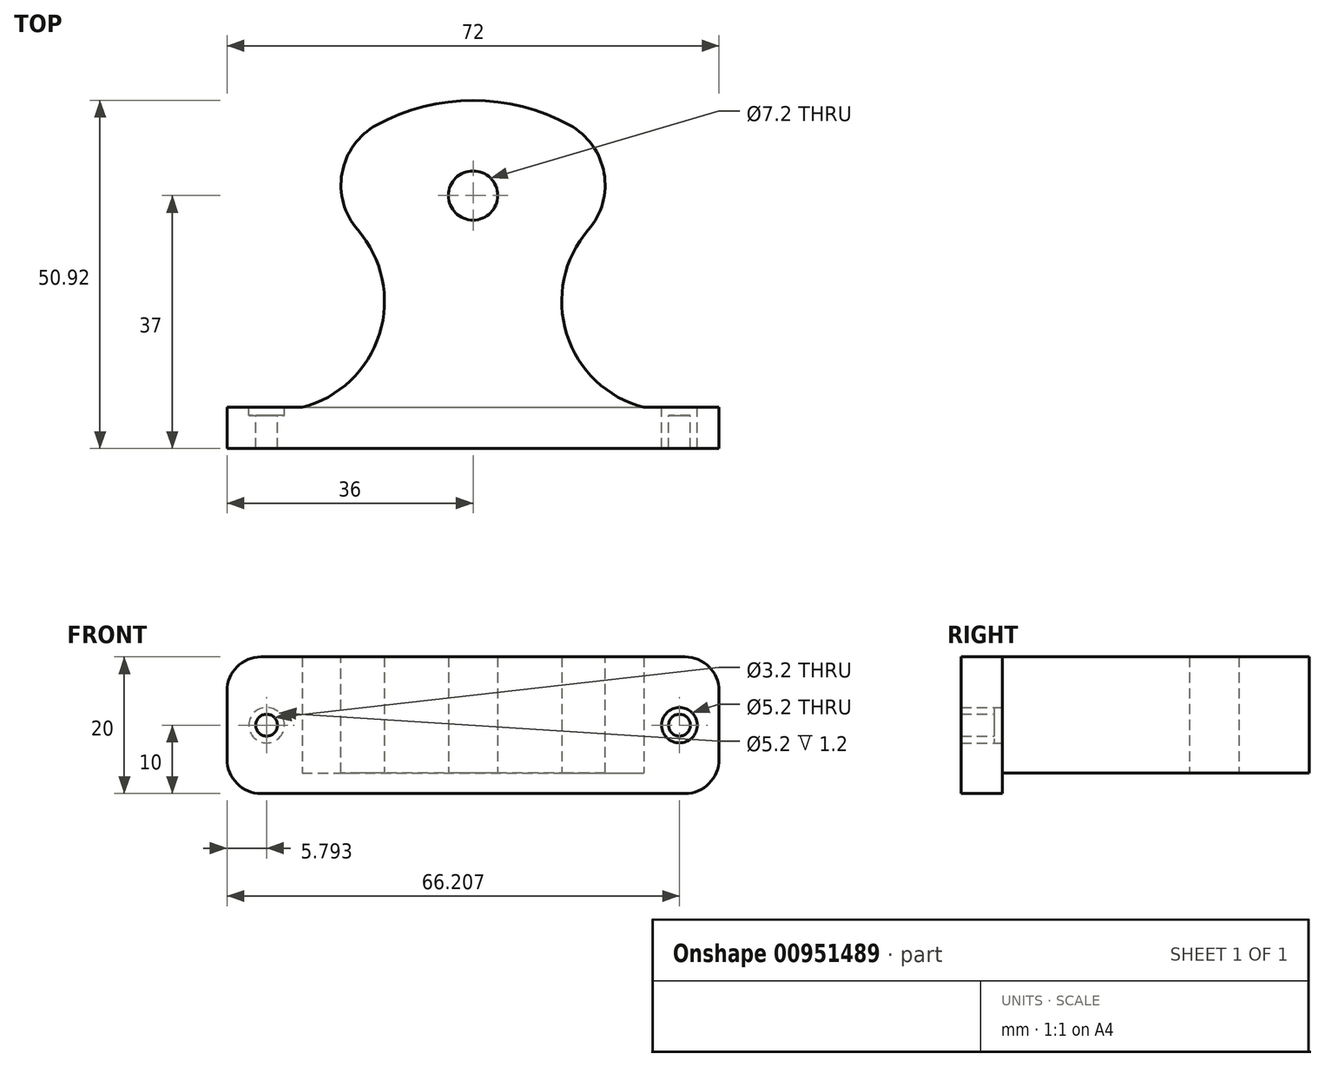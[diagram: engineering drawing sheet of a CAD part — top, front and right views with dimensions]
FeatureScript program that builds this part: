
annotation { "Feature Type Name" : "Feature", "Feature Type Description" : "" }
export const myFeature = defineFeature(function(context is Context, id is Id, definition is map)
    precondition{}
    {
        {
            var Q0;
            Q0=qCreatedBy(makeId("Top.planeOp"),FACE);
            var sketch = newSketch(context, id + "F0", { "sketchPlane" : qUnion([Q0])});
            skLineSegment(sketch, "E0.bottom", {"start": v(-25, 15.5) * mm, "end": v(25, 15.5) * mm});
            skLineSegment(sketch, "E0.top", {"start": v(-25, -15.5) * mm, "end": v(25, -15.5) * mm});
            skLineSegment(sketch, "E0.left", {"start": v(-25, 15.5) * mm, "end": v(-25, -15.5) * mm});
            skLineSegment(sketch, "E0.right", {"start": v(25, 15.5) * mm, "end": v(25, -15.5) * mm});
            skPoint(sketch, "E0.middle", {"position": v(0, 0) * mm});
            skCircle(sketch, "E1", {"center": v(0, 0) * mm, "radius": 29.42 * mm});
            skPoint(sketch, "E2", {"position": v(0, 15.5) * mm});
            skCircle(sketch, "E3", {"center": v(0, 15.5) * mm, "radius": 2.5 * mm});
            skLineSegment(sketch, "E4.bottom", {"start": v(-36, -15.5) * mm, "end": v(36, -15.5) * mm});
            skLineSegment(sketch, "E4.top", {"start": v(-36, -21.5) * mm, "end": v(36, -21.5) * mm});
            skLineSegment(sketch, "E4.left", {"start": v(-36, -15.5) * mm, "end": v(-36, -21.5) * mm});
            skLineSegment(sketch, "E4.right", {"start": v(36, -15.5) * mm, "end": v(36, -21.5) * mm});
            skPoint(sketch, "E4.middle", {"position": v(0, -18.5) * mm});
            skArc(sketch, "E5", {"start": v(-25, -15.5) * mm, "mid": v(-12.97, 0) * mm, "end": v(-25, 15.5) * mm});
            skArc(sketch, "E6.MirrorCS", {"start": v(25, -15.5) * mm, "mid": v(12.97, 0) * mm, "end": v(25, 15.5) * mm});
            skCircle(sketch, "E7", {"center": v(0, 15.5) * mm, "radius": 3.6 * mm});
            skSolve(sketch);
        }
        {
            var Q0;
            Q0=makeQuery(id+"F0.imprint","IMPRINT",FACE,{"disambiguationData":[TD([[makeQuery(id+"F0.imprint","IMPRINT",EDGE,{"derivedFrom":sQuery(id+"F0.wireOp",EDGE,"E0.top")}),1.0]])]});
            var Q1;
            {var subQ0=sQuery(id+"F0.wireOp",EDGE,"E7");var subQ1=sQuery(id+"F0.wireOp",EDGE,"E0.bottom");var subQ2=makeQuery(id+"F0.imprint","INTERSECT",VERTEX,{"disambiguationData":[OD(0.0)],"derivedFrom":[subQ1,subQ0]});Q1=makeQuery(id+"F0.imprint","IMPRINT",FACE,{"disambiguationData":[TD([[makeQuery(id+"F0.imprint","IMPRINT",EDGE,{"disambiguationData":[TD([[subQ2,1.0]])],"derivedFrom":subQ1}),1.0]])]});}
            var Q2;
            {var subQ5=sQuery(id+"F0.wireOp",EDGE,"E4.left");Q2=makeQuery(id+"F0.imprint","IMPRINT",FACE,{"disambiguationData":[TD([[makeQuery(id+"F0.imprint","IMPRINT",EDGE,{"derivedFrom":subQ5}),1.0]])]});}
            var Q3;
            {var subQ0=sQuery(id+"F0.wireOp",EDGE,"E0.top");Q3=makeQuery(id+"F0.imprint","IMPRINT",FACE,{"disambiguationData":[TD([[makeQuery(id+"F0.imprint","IMPRINT",EDGE,{"derivedFrom":subQ0}),-1.0]])]});}
            var Q4;
            {var subQ5=sQuery(id+"F0.wireOp",EDGE,"E4.right");Q4=makeQuery(id+"F0.imprint","IMPRINT",FACE,{"disambiguationData":[TD([[makeQuery(id+"F0.imprint","IMPRINT",EDGE,{"derivedFrom":subQ5}),-1.0]])]});}
            var Q5;
            Q5=makeQuery(id+"F0.imprint","IMPRINT",FACE,{"disambiguationData":[TD([[makeQuery(id+"F0.imprint","IMPRINT",EDGE,{"derivedFrom":sQuery(id+"F0.wireOp",EDGE,"E0.top")}),1.0]])]});
            var Q6;
            {var subQ0=sQuery(id+"F0.wireOp",EDGE,"E7");var subQ1=sQuery(id+"F0.wireOp",EDGE,"E0.bottom");var subQ2=makeQuery(id+"F0.imprint","INTERSECT",VERTEX,{"disambiguationData":[OD(0.0)],"derivedFrom":[subQ1,subQ0]});Q6=makeQuery(id+"F0.imprint","IMPRINT",FACE,{"disambiguationData":[TD([[makeQuery(id+"F0.imprint","IMPRINT",EDGE,{"disambiguationData":[TD([[subQ2,-1.0]])],"derivedFrom":subQ0}),-1.0]])]});}
            var Q7;
            {var subQ0=sQuery(id+"F0.wireOp",EDGE,"E7");var subQ1=sQuery(id+"F0.wireOp",EDGE,"E0.bottom");var subQ2=makeQuery(id+"F0.imprint","INTERSECT",VERTEX,{"disambiguationData":[OD(0.0)],"derivedFrom":[subQ1,subQ0]});Q7=makeQuery(id+"F0.imprint","IMPRINT",FACE,{"disambiguationData":[TD([[makeQuery(id+"F0.imprint","IMPRINT",EDGE,{"disambiguationData":[TD([[subQ2,1.0]])],"derivedFrom":subQ1}),-1.0]])]});}
            extrude(context, id + "F1", {"entities" : qUnion([Q0, Q1, Q2, Q3, Q4, Q5, Q6, Q7]), "depth" : 20 * mm, "offsetDistance" : 25 * mm});
        }
        {
            var Q0;
            Q0=makeQuery(id+"F1.opExtrude","SWEPT_EDGE",EDGE,{"disambiguationData":[OSD([sQuery(id+"F0.wireOp",EDGE,"E0.bottom"),sQuery(id+"F0.wireOp",EDGE,"E0.right"),sQuery(id+"F0.wireOp",EDGE,"E1"),sQuery(id+"F0.wireOp",EDGE,"E6.MirrorCS")])]});
            var Q1;
            Q1=makeQuery(id+"F1.opExtrude","SWEPT_EDGE",EDGE,{"disambiguationData":[OSD([sQuery(id+"F0.wireOp",EDGE,"E0.bottom"),sQuery(id+"F0.wireOp",EDGE,"E0.left"),sQuery(id+"F0.wireOp",EDGE,"E1"),sQuery(id+"F0.wireOp",EDGE,"E5")])]});
            fillet(context, id + "F2", {"entities" : qUnion([Q0, Q1]), "radius" : 10 * mm, "tangentPropagation" : true, "allowEdgeOverflow" : false});
        }
        {
            var Q0;
            {var subQ0=sQuery(id+"F0.wireOp",EDGE,"E4.bottom");Q0=makeQuery(id+"F1.opExtrude","SWEPT_FACE",FACE,{"disambiguationData":[OSD([subQ0]),TDD([makeQuery(id+"F0.imprint","IMPRINT",EDGE,{"disambiguationData":[TD([[makeQuery(id+"F0.imprint","INTERSECT",VERTEX,{"derivedFrom":[subQ0,sQuery(id+"F0.wireOp",EDGE,"E4.left")]}),-1.0]])],"derivedFrom":subQ0})])]});}
            var sketch = newSketch(context, id + "F3", { "sketchPlane" : qUnion([Q0])});
            skCircle(sketch, "E8", {"center": v(30.2, 10) * mm, "radius": 1.6 * mm});
            skPoint(sketch, "E8.centerSnap0", {"position": v(25, 10) * mm});
            skCircle(sketch, "E9.MirrorC", {"center": v(-30.2, 10) * mm, "radius": 1.6 * mm});
            skCircle(sketch, "E10", {"center": v(-30.2, 10) * mm, "radius": 2.6 * mm});
            skCircle(sketch, "E11.MirrorC", {"center": v(30.2, 10) * mm, "radius": 2.6 * mm});
            skSolve(sketch);
        }
        {
            var Q0;
            Q0=makeQuery(id+"F3.imprint","IMPRINT",FACE,{"disambiguationData":[TD([[makeQuery(id+"F3.imprint","IMPRINT",EDGE,{"derivedFrom":sQuery(id+"F3.wireOp",EDGE,"E8")}),1.0]])]});
            var Q1;
            Q1=makeQuery(id+"F3.imprint","IMPRINT",FACE,{"disambiguationData":[TD([[makeQuery(id+"F3.imprint","IMPRINT",EDGE,{"derivedFrom":sQuery(id+"F3.wireOp",EDGE,"E9.MirrorC")}),-1.0]])]});
            extrude(context, id + "F4", {"entities" : qUnion([Q0, Q1]), "operationType" : NewBodyOperationType.REMOVE, "oppositeDirection" : true, "depth" : 25 * mm, "offsetDistance" : 25 * mm});
        }
        {
            var Q0;
            Q0=makeQuery(id+"F1.opExtrude","CAP_EDGE",EDGE,{"disambiguationData":[OSD([sQuery(id+"F0.wireOp",EDGE,"E4.left")])],"isStart":false});
            var Q1;
            Q1=makeQuery(id+"F1.opExtrude","CAP_EDGE",EDGE,{"disambiguationData":[OSD([sQuery(id+"F0.wireOp",EDGE,"E4.right")])],"isStart":false});
            var Q2;
            Q2=makeQuery(id+"F1.opExtrude","CAP_EDGE",EDGE,{"disambiguationData":[OSD([sQuery(id+"F0.wireOp",EDGE,"E4.right")])],"isStart":true});
            var Q3;
            Q3=makeQuery(id+"F1.opExtrude","CAP_EDGE",EDGE,{"disambiguationData":[OSD([sQuery(id+"F0.wireOp",EDGE,"E4.left")])],"isStart":true});
            fillet(context, id + "F5", {"entities" : qUnion([Q0, Q1, Q2, Q3]), "radius" : 5 * mm, "tangentPropagation" : true, "allowEdgeOverflow" : false});
        }
        {
            var Q0;
            {var subQ0=sQuery(id+"F0.wireOp",EDGE,"E7");var subQ1=sQuery(id+"F0.wireOp",EDGE,"E0.bottom");var subQ2=makeQuery(id+"F0.imprint","INTERSECT",VERTEX,{"disambiguationData":[OD(0.0)],"derivedFrom":[subQ1,subQ0]});Q0=makeQuery(id+"F0.imprint","IMPRINT",FACE,{"disambiguationData":[TD([[makeQuery(id+"F0.imprint","IMPRINT",EDGE,{"disambiguationData":[TD([[subQ2,1.0]])],"derivedFrom":subQ1}),1.0]])]});}
            var Q1;
            {var subQ0=sQuery(id+"F0.wireOp",EDGE,"E7");var subQ1=sQuery(id+"F0.wireOp",EDGE,"E0.bottom");var subQ2=makeQuery(id+"F0.imprint","INTERSECT",VERTEX,{"disambiguationData":[OD(0.0)],"derivedFrom":[subQ1,subQ0]});Q1=makeQuery(id+"F0.imprint","IMPRINT",FACE,{"disambiguationData":[TD([[makeQuery(id+"F0.imprint","IMPRINT",EDGE,{"disambiguationData":[TD([[subQ2,1.0]])],"derivedFrom":subQ1}),-1.0]])]});}
            var Q2;
            Q2=sQuery(id+"F0.wireOp",EDGE,"E7");
            extrude(context, id + "F6", {"entities" : qUnion([Q0, Q1]), "operationType" : NewBodyOperationType.REMOVE, "surfaceEntities" : qUnion([Q2]), "depth" : 3 * mm, "offsetDistance" : 25 * mm});
        }
        {
            var Q0;
            Q0=makeQuery(id+"F3.imprint","IMPRINT",FACE,{"disambiguationData":[TD([[makeQuery(id+"F3.imprint","IMPRINT",EDGE,{"derivedFrom":sQuery(id+"F3.wireOp",EDGE,"E9.MirrorC")}),1.0]])]});
            var Q1;
            Q1=makeQuery(id+"F3.imprint","IMPRINT",FACE,{"disambiguationData":[TD([[makeQuery(id+"F3.imprint","IMPRINT",EDGE,{"derivedFrom":sQuery(id+"F3.wireOp",EDGE,"E8")}),-1.0]])]});
            extrude(context, id + "F7", {"entities" : qUnion([Q0, Q1]), "operationType" : NewBodyOperationType.REMOVE, "oppositeDirection" : true, "depth" : 1.2 * mm, "offsetDistance" : 25 * mm});
        }
    });
